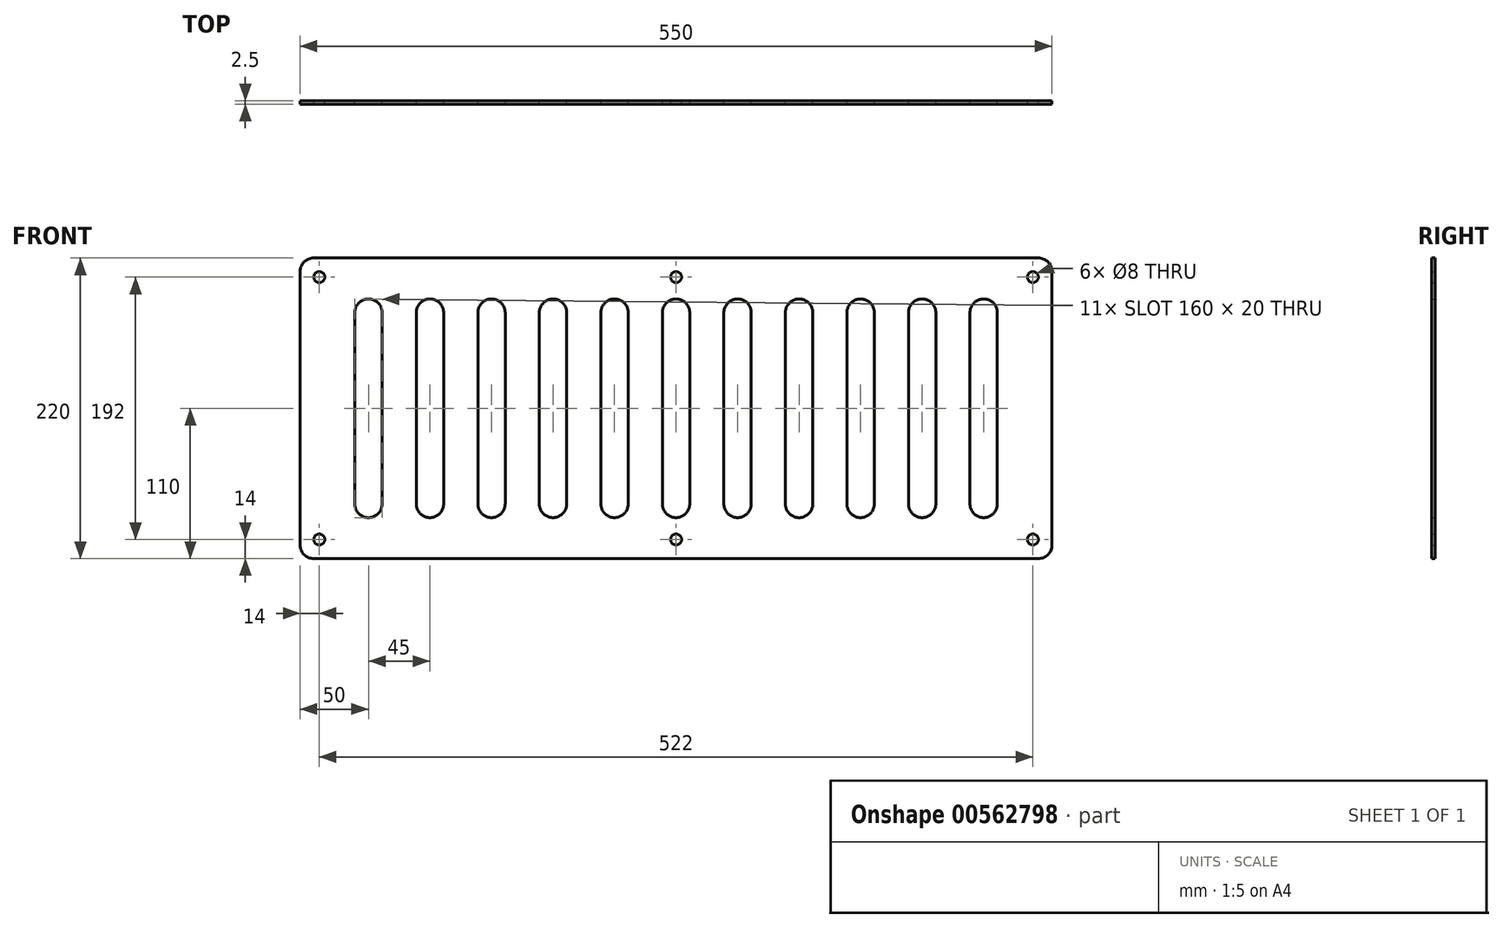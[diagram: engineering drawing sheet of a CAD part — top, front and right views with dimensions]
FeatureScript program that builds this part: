
annotation { "Feature Type Name" : "Feature", "Feature Type Description" : "" }
export const myFeature = defineFeature(function(context is Context, id is Id, definition is map)
    precondition{}
    {
        {
            var Q0;
            Q0=qCreatedBy(makeId("Front.planeOp"),FACE);
            var sketch = newSketch(context, id + "F0", { "sketchPlane" : qUnion([Q0])});
            skLineSegment(sketch, "E0.bottom", {"start": v(10, 0) * mm, "end": v(540, 0) * mm});
            skLineSegment(sketch, "E0.top", {"start": v(10, 220) * mm, "end": v(540, 220) * mm});
            skLineSegment(sketch, "E0.left", {"start": v(0, 10) * mm, "end": v(0, 210) * mm});
            skLineSegment(sketch, "E0.right", {"start": v(550, 10) * mm, "end": v(550, 210) * mm});
            skArc(sketch, "E1", {"start": v(60, 180) * mm, "mid": v(49.96, 190) * mm, "end": v(40, 179.92) * mm});
            skArc(sketch, "E2", {"start": v(40, 40.08) * mm, "mid": v(49.96, 30) * mm, "end": v(60, 40) * mm});
            skLineSegment(sketch, "E3", {"start": v(40, 179.92) * mm, "end": v(40, 39.92) * mm});
            skLineSegment(sketch, "E4", {"start": v(60, 180) * mm, "end": v(60, 40) * mm});
            skLineSegment(sketch, "E5.1.0.0", {"start": v(85, 179.92) * mm, "end": v(85, 39.92) * mm});
            skLineSegment(sketch, "E5.1.0.1", {"start": v(105, 180) * mm, "end": v(105, 40) * mm});
            skArc(sketch, "E5.1.0.2", {"start": v(105, 180) * mm, "mid": v(94.96, 190) * mm, "end": v(85, 179.92) * mm});
            skArc(sketch, "E5.1.0.3", {"start": v(85, 40.08) * mm, "mid": v(94.96, 30) * mm, "end": v(105, 40) * mm});
            skLineSegment(sketch, "E5.2.0.0", {"start": v(130, 179.92) * mm, "end": v(130, 39.92) * mm});
            skLineSegment(sketch, "E5.2.0.1", {"start": v(150, 180) * mm, "end": v(150, 40) * mm});
            skArc(sketch, "E5.2.0.2", {"start": v(150, 180) * mm, "mid": v(139.96, 190) * mm, "end": v(130, 179.92) * mm});
            skArc(sketch, "E5.2.0.3", {"start": v(130, 40.08) * mm, "mid": v(139.96, 30) * mm, "end": v(150, 40) * mm});
            skLineSegment(sketch, "E5.3.0.0", {"start": v(175, 179.92) * mm, "end": v(175, 39.92) * mm});
            skLineSegment(sketch, "E5.3.0.1", {"start": v(195, 180) * mm, "end": v(195, 40) * mm});
            skArc(sketch, "E5.3.0.2", {"start": v(195, 180) * mm, "mid": v(184.96, 190) * mm, "end": v(175, 179.92) * mm});
            skArc(sketch, "E5.3.0.3", {"start": v(175, 40.08) * mm, "mid": v(184.96, 30) * mm, "end": v(195, 40) * mm});
            skLineSegment(sketch, "E5.4.0.0", {"start": v(220, 179.92) * mm, "end": v(220, 39.92) * mm});
            skLineSegment(sketch, "E5.4.0.1", {"start": v(240, 180) * mm, "end": v(240, 40) * mm});
            skArc(sketch, "E5.4.0.2", {"start": v(240, 180) * mm, "mid": v(229.96, 190) * mm, "end": v(220, 179.92) * mm});
            skArc(sketch, "E5.4.0.3", {"start": v(220, 40.08) * mm, "mid": v(229.96, 30) * mm, "end": v(240, 40) * mm});
            skLineSegment(sketch, "E5.5.0.0", {"start": v(265, 179.92) * mm, "end": v(265, 39.92) * mm});
            skLineSegment(sketch, "E5.5.0.1", {"start": v(285, 180) * mm, "end": v(285, 40) * mm});
            skArc(sketch, "E5.5.0.2", {"start": v(285, 180) * mm, "mid": v(274.96, 190) * mm, "end": v(265, 179.92) * mm});
            skArc(sketch, "E5.5.0.3", {"start": v(265, 40.08) * mm, "mid": v(274.96, 30) * mm, "end": v(285, 40) * mm});
            skLineSegment(sketch, "E5.6.0.0", {"start": v(310, 179.92) * mm, "end": v(310, 39.92) * mm});
            skLineSegment(sketch, "E5.6.0.1", {"start": v(330, 180) * mm, "end": v(330, 40) * mm});
            skArc(sketch, "E5.6.0.2", {"start": v(330, 180) * mm, "mid": v(319.96, 190) * mm, "end": v(310, 179.92) * mm});
            skArc(sketch, "E5.6.0.3", {"start": v(310, 40.08) * mm, "mid": v(319.96, 30) * mm, "end": v(330, 40) * mm});
            skLineSegment(sketch, "E5.7.0.0", {"start": v(355, 179.92) * mm, "end": v(355, 39.92) * mm});
            skLineSegment(sketch, "E5.7.0.1", {"start": v(375, 180) * mm, "end": v(375, 40) * mm});
            skArc(sketch, "E5.7.0.2", {"start": v(375, 180) * mm, "mid": v(364.96, 190) * mm, "end": v(355, 179.92) * mm});
            skArc(sketch, "E5.7.0.3", {"start": v(355, 40.08) * mm, "mid": v(364.96, 30) * mm, "end": v(375, 40) * mm});
            skLineSegment(sketch, "E5.8.0.0", {"start": v(400, 179.92) * mm, "end": v(400, 39.92) * mm});
            skLineSegment(sketch, "E5.8.0.1", {"start": v(420, 180) * mm, "end": v(420, 40) * mm});
            skArc(sketch, "E5.8.0.2", {"start": v(420, 180) * mm, "mid": v(409.96, 190) * mm, "end": v(400, 179.92) * mm});
            skArc(sketch, "E5.8.0.3", {"start": v(400, 40.08) * mm, "mid": v(409.96, 30) * mm, "end": v(420, 40) * mm});
            skLineSegment(sketch, "E5.9.0.0", {"start": v(445, 179.92) * mm, "end": v(445, 39.92) * mm});
            skLineSegment(sketch, "E5.9.0.1", {"start": v(465, 180) * mm, "end": v(465, 40) * mm});
            skArc(sketch, "E5.9.0.2", {"start": v(465, 180) * mm, "mid": v(454.96, 190) * mm, "end": v(445, 179.92) * mm});
            skArc(sketch, "E5.9.0.3", {"start": v(445, 40.08) * mm, "mid": v(454.96, 30) * mm, "end": v(465, 40) * mm});
            skLineSegment(sketch, "E5.10.0.0", {"start": v(490, 179.92) * mm, "end": v(490, 39.92) * mm});
            skLineSegment(sketch, "E5.10.0.1", {"start": v(510, 180) * mm, "end": v(510, 40) * mm});
            skArc(sketch, "E5.10.0.2", {"start": v(510, 180) * mm, "mid": v(499.96, 190) * mm, "end": v(490, 179.92) * mm});
            skArc(sketch, "E5.10.0.3", {"start": v(490, 40.08) * mm, "mid": v(499.96, 30) * mm, "end": v(510, 40) * mm});
            skLineSegment(sketch, "E5.direction1", {"start": v(40, 39.92) * mm, "end": v(85, 39.92) * mm, "construction": true});
            skPoint(sketch, "E6.visualSharp", {"position": v(0, 220) * mm});
            skArc(sketch, "E6.filletArc", {"start": v(10, 220) * mm, "mid": v(2.93, 217.07) * mm, "end": v(0, 210) * mm});
            skPoint(sketch, "E7.visualSharp", {"position": v(0, 0) * mm});
            skArc(sketch, "E7.filletArc", {"start": v(0, 10) * mm, "mid": v(2.93, 2.93) * mm, "end": v(10, 0) * mm});
            skPoint(sketch, "E8.visualSharp", {"position": v(550, 220) * mm});
            skArc(sketch, "E8.filletArc", {"start": v(550, 210) * mm, "mid": v(547.07, 217.07) * mm, "end": v(540, 220) * mm});
            skPoint(sketch, "E9.visualSharp", {"position": v(550, 0) * mm});
            skArc(sketch, "E9.filletArc", {"start": v(540, 0) * mm, "mid": v(547.07, 2.93) * mm, "end": v(550, 10) * mm});
            skCircle(sketch, "E10", {"center": v(536, 206) * mm, "radius": 4 * mm});
            skCircle(sketch, "E11", {"center": v(536, 14) * mm, "radius": 4 * mm});
            skCircle(sketch, "E12", {"center": v(14, 14) * mm, "radius": 4 * mm});
            skCircle(sketch, "E13", {"center": v(14, 206) * mm, "radius": 4 * mm});
            skCircle(sketch, "E14", {"center": v(275, 206) * mm, "radius": 4 * mm});
            skCircle(sketch, "E15", {"center": v(275, 14) * mm, "radius": 4 * mm});
            skSolve(sketch);
        }
        {
            var Q0;
            Q0=makeQuery(id+"F0.imprint","IMPRINT",FACE,{"disambiguationData":[TD([[makeQuery(id+"F0.imprint","IMPRINT",EDGE,{"derivedFrom":sQuery(id+"F0.wireOp",EDGE,"E0.bottom")}),1.0]])]});
            extrude(context, id + "F1", {"entities" : qUnion([Q0]), "depth" : 2.5 * mm, "offsetDistance" : 25 * mm});
        }
    });
